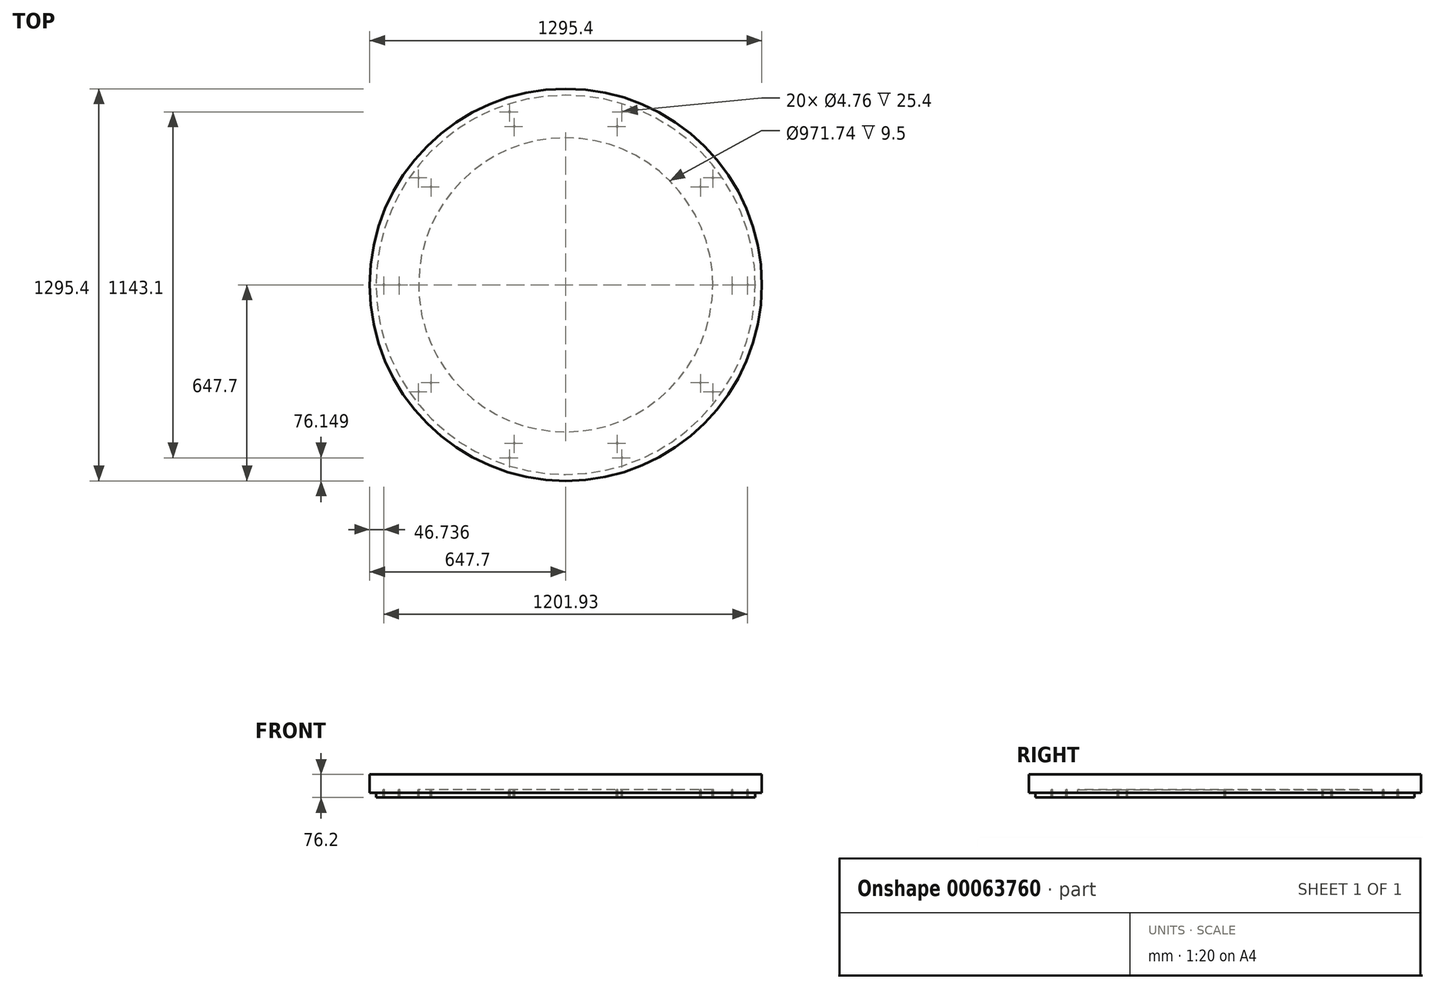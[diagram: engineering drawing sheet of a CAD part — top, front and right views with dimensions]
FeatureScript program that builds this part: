
annotation { "Feature Type Name" : "Feature", "Feature Type Description" : "" }
export const myFeature = defineFeature(function(context is Context, id is Id, definition is map)
    precondition{}
    {
        {
            assignVariable(context, id + "F0", {"name" : "H", "anyValue" : 15});
        }
        {
            assignVariable(context, id + "F1", {"name" : "S", "anyValue" : 10});
        }
        {
            var Q0;
            Q0=qCreatedBy(makeId("Top.planeOp"),FACE);
            var sketch = newSketch(context, id + "F2", { "sketchPlane" : qUnion([Q0])});
            skCircle(sketch, "E0", {"center": v(0, 0) * mm, "radius": 647.7 * mm});
            skCircle(sketch, "E1", {"center": v(0, 0) * mm, "radius": 635 * mm});
            skCircle(sketch, "E2.0", {"center": v(0, 0) * mm, "radius": 626.36 * mm});
            skSolve(sketch);
        }
        {
            var Q0;
            Q0=makeQuery(id+"F2.imprint","IMPRINT",FACE,{"disambiguationData":[TD([[makeQuery(id+"F2.imprint","IMPRINT",EDGE,{"derivedFrom":sQuery(id+"F2.wireOp",EDGE,"E1")}),1.0]])]});
            var Q1;
            Q1=sQuery(id+"F2.wireOp",EDGE,"E1");
            var Q2;
            Q2=sQuery(id+"F2.wireOp",EDGE,"E2.0");
            extrude(context, id + "F3", {"entities" : qUnion([Q0]), "surfaceEntities" : qUnion([Q1, Q2]), "depth" : (getVariable(context, 'H') - 5.5) * mm});
        }
        {
            var Q0;
            Q0=makeQuery(id+"F3.opExtrude","CAP_FACE",FACE,{"disambiguationData":[OSD([sQuery(id+"F2.wireOp",EDGE,"E1"),sQuery(id+"F2.wireOp",EDGE,"E2.0")])],"isStart":false});
            var sketch = newSketch(context, id + "F4", { "sketchPlane" : qUnion([Q0])});
            skCircle(sketch, "E3.0", {"center": v(0, 0) * mm, "radius": 626.36 * mm});
            skSolve(sketch);
        }
        {
            var Q0;
            Q0=qSketchRegion(id+"F4",true);
            extrude(context, id + "F5", {"entities" : qUnion([Q0]), "oppositeDirection" : true, "depth" : 25.4 * mm});
        }
        {
            var Q0;
            Q0=makeQuery(id+"F5.opExtrude","CAP_FACE",FACE,{"disambiguationData":[OSD([sQuery(id+"F4.wireOp",EDGE,"E3.0")])],"isStart":true});
            var sketch = newSketch(context, id + "F6", { "sketchPlane" : qUnion([Q0])});
            skLineSegment(sketch, "E4", {"start": v(-626.36, 0) * mm, "end": v(0, 0) * mm, "construction": true});
            skCircle(sketch, "E5.0", {"center": v(0, 0) * mm, "radius": 600.96 * mm, "construction": true});
            skCircle(sketch, "E6.0", {"center": v(0, 0) * mm, "radius": 550.16 * mm, "construction": true});
            skPoint(sketch, "E7", {"position": v(-600.96, 0) * mm});
            skPoint(sketch, "E8", {"position": v(-550.16, 0) * mm});
            skPoint(sketch, "E9.1.0", {"position": v(-445.1, -323.38) * mm});
            skPoint(sketch, "E9.1.1", {"position": v(-486.2, -353.24) * mm});
            skPoint(sketch, "E9.2.0", {"position": v(-170.01, -523.24) * mm});
            skPoint(sketch, "E9.2.1", {"position": v(-185.7, -571.55) * mm});
            skPoint(sketch, "E9.3.0", {"position": v(170.01, -523.24) * mm});
            skPoint(sketch, "E9.3.1", {"position": v(185.7, -571.55) * mm});
            skPoint(sketch, "E9.4.0", {"position": v(445.1, -323.38) * mm});
            skPoint(sketch, "E9.4.1", {"position": v(486.2, -353.24) * mm});
            skPoint(sketch, "E10.0.5.0", {"position": v(550.16, 0) * mm});
            skPoint(sketch, "E10.1.5.0", {"position": v(600.96, 0) * mm});
            skPoint(sketch, "E11.0.6.0", {"position": v(445.1, 323.38) * mm});
            skPoint(sketch, "E11.1.6.0", {"position": v(486.2, 353.24) * mm});
            skPoint(sketch, "E12.0.7.0", {"position": v(170.01, 523.24) * mm});
            skPoint(sketch, "E12.1.7.0", {"position": v(185.7, 571.55) * mm});
            skPoint(sketch, "E12.0.8.0", {"position": v(-170.01, 523.24) * mm});
            skPoint(sketch, "E12.1.8.0", {"position": v(-185.7, 571.55) * mm});
            skPoint(sketch, "E12.0.9.0", {"position": v(-445.1, 323.38) * mm});
            skPoint(sketch, "E12.1.9.0", {"position": v(-486.2, 353.24) * mm});
            skSolve(sketch);
        }
        {
            var Q0;
            Q0=sQuery(id+"F6.wireOp",VERTEX,"E7");
            var Q1;
            Q1=sQuery(id+"F6.wireOp",VERTEX,"E8");
            var Q2;
            Q2=sQuery(id+"F6.wireOp",VERTEX,"E9.4.1");
            var Q3;
            Q3=sQuery(id+"F6.wireOp",VERTEX,"E9.4.0");
            var Q4;
            Q4=sQuery(id+"F6.wireOp",VERTEX,"E9.3.0");
            var Q5;
            Q5=sQuery(id+"F6.wireOp",VERTEX,"E9.3.1");
            var Q6;
            Q6=sQuery(id+"F6.wireOp",VERTEX,"E9.2.0");
            var Q7;
            Q7=sQuery(id+"F6.wireOp",VERTEX,"E9.2.1");
            var Q8;
            Q8=sQuery(id+"F6.wireOp",VERTEX,"E9.1.1");
            var Q9;
            Q9=sQuery(id+"F6.wireOp",VERTEX,"E9.1.0");
            var Q10;
            Q10=sQuery(id+"F6.wireOp",VERTEX,"E10.0.5.0");
            var Q11;
            Q11=sQuery(id+"F6.wireOp",VERTEX,"E10.1.5.0");
            var Q12;
            Q12=sQuery(id+"F6.wireOp",VERTEX,"E11.1.6.0");
            var Q13;
            Q13=sQuery(id+"F6.wireOp",VERTEX,"E11.0.6.0");
            var Q14;
            Q14=sQuery(id+"F6.wireOp",VERTEX,"E12.1.9.0");
            var Q15;
            Q15=sQuery(id+"F6.wireOp",VERTEX,"E12.0.9.0");
            var Q16;
            Q16=sQuery(id+"F6.wireOp",VERTEX,"E12.1.8.0");
            var Q17;
            Q17=sQuery(id+"F6.wireOp",VERTEX,"E12.0.8.0");
            var Q18;
            Q18=sQuery(id+"F6.wireOp",VERTEX,"E12.0.7.0");
            var Q19;
            Q19=sQuery(id+"F6.wireOp",VERTEX,"E12.1.7.0");
            var Q20;
            Q20=makeQuery(id+"F5.opExtrude","SWEPT_BODY",BODY,{"disambiguationData":[OSD([sQuery(id+"F4.wireOp",EDGE,"E3.0")])]});
            hole(context, id + "F7", {"style" : HoleStyle.C_SINK, "holeDiameter" : 4.76 * mm, "cSinkDiameter" : 8.43 * mm, "endStyle" : HoleEndStyle.THROUGH, "locations" : qUnion([Q0, Q1, Q2, Q3, Q4, Q5, Q6, Q7, Q8, Q9, Q10, Q11, Q12, Q13, Q14, Q15, Q16, Q17, Q18, Q19]), "scope" : qUnion([Q20]), "cSinkAngle" : 90 * degree});
        }
        {
            var Q0;
            Q0=makeQuery(id+"F5.opExtrude","SWEPT_BODY",BODY,{"disambiguationData":[OSD([sQuery(id+"F4.wireOp",EDGE,"E3.0")])]});
            var Q1;
            Q1=qCreatedBy(makeId("Top.planeOp"),FACE);
            mirror(context, id + "F8", {"entities" : qUnion([Q0]), "mirrorPlane" : qUnion([Q1])});
        }
        {
            var Q0;
            Q0=makeQuery(id+"F8.opPattern","COPY",BODY,{"derivedFrom":makeQuery(id+"F5.opExtrude","SWEPT_BODY",BODY,{"disambiguationData":[OSD([sQuery(id+"F4.wireOp",EDGE,"E3.0")])]}),"instanceName":"1"});
            var Q1;
            Q1=makeQuery(id+"F5.opExtrude","CAP_FACE",FACE,{"disambiguationData":[OSD([sQuery(id+"F4.wireOp",EDGE,"E3.0")])],"isStart":true});
            transform(context, id + "F9", {"entities" : qUnion([Q0]), "transformType" : TransformType.TRANSLATION_3D, "dx" : 0 * mm, "dy" : 0 * mm, "dz" : (getVariable(context, 'H') - 5.5) * mm, "makeCopy" : false});
        }
        {
            var Q0;
            Q0=makeQuery(id+"F8.opPattern","COPY",FACE,{"derivedFrom":makeQuery(id+"F5.opExtrude","CAP_FACE",FACE,{"disambiguationData":[OSD([sQuery(id+"F4.wireOp",EDGE,"E3.0")])],"isStart":true}),"instanceName":"1"});
            var sketch = newSketch(context, id + "F10", { "sketchPlane" : qUnion([Q0])});
            skCircle(sketch, "E13.0", {"center": v(0, 0) * mm, "radius": 608.1 * mm, "construction": true});
            skCircle(sketch, "E14.0", {"center": v(0, 0) * mm, "radius": 571.6 * mm, "construction": true});
            skCircle(sketch, "E15.0", {"center": v(0, 0) * mm, "radius": 535.08 * mm, "construction": true});
            skLineSegment(sketch, "E16", {"start": v(0, 0) * mm, "end": v(0, 608.1) * mm, "construction": true});
            skLineSegment(sketch, "E17.0", {"start": v(22.23, 0) * mm, "end": v(22.23, 265.2) * mm, "construction": true});
            skLineSegment(sketch, "E18.0", {"start": v(-22.23, 0) * mm, "end": v(-22.23, 265.2) * mm, "construction": true});
            skPoint(sketch, "E19", {"position": v(-22.23, 571.16) * mm});
            skPoint(sketch, "E20", {"position": v(-22.23, 534.62) * mm});
            skPoint(sketch, "E21", {"position": v(22.23, 534.62) * mm});
            skPoint(sketch, "E22", {"position": v(22.23, 571.16) * mm});
            skPoint(sketch, "E23", {"position": v(22.23, 607.7) * mm});
            skPoint(sketch, "E24", {"position": v(-22.23, 607.7) * mm});
            skPoint(sketch, "E25.1.0", {"position": v(-515.32, 144.07) * mm});
            skPoint(sketch, "E25.1.1", {"position": v(-550.08, 155.36) * mm});
            skPoint(sketch, "E25.1.2", {"position": v(-584.83, 166.65) * mm});
            skPoint(sketch, "E25.1.3", {"position": v(-571.1, 208.93) * mm});
            skPoint(sketch, "E25.1.4", {"position": v(-536.34, 197.64) * mm});
            skPoint(sketch, "E25.1.5", {"position": v(-501.59, 186.34) * mm});
            skPoint(sketch, "E25.2.0", {"position": v(-296.26, -445.58) * mm});
            skPoint(sketch, "E25.2.1", {"position": v(-317.74, -475.14) * mm});
            skPoint(sketch, "E25.2.2", {"position": v(-339.22, -504.7) * mm});
            skPoint(sketch, "E25.2.3", {"position": v(-375.18, -478.58) * mm});
            skPoint(sketch, "E25.2.4", {"position": v(-353.7, -449.02) * mm});
            skPoint(sketch, "E25.2.5", {"position": v(-332.22, -419.45) * mm});
            skPoint(sketch, "E25.3.0", {"position": v(332.22, -419.45) * mm});
            skPoint(sketch, "E25.3.1", {"position": v(353.7, -449.02) * mm});
            skPoint(sketch, "E25.3.2", {"position": v(375.18, -478.58) * mm});
            skPoint(sketch, "E25.3.3", {"position": v(339.22, -504.7) * mm});
            skPoint(sketch, "E25.3.4", {"position": v(317.74, -475.14) * mm});
            skPoint(sketch, "E25.3.5", {"position": v(296.26, -445.58) * mm});
            skPoint(sketch, "E25.4.0", {"position": v(501.59, 186.34) * mm});
            skPoint(sketch, "E25.4.1", {"position": v(536.34, 197.64) * mm});
            skPoint(sketch, "E25.4.2", {"position": v(571.1, 208.93) * mm});
            skPoint(sketch, "E25.4.3", {"position": v(584.83, 166.65) * mm});
            skPoint(sketch, "E25.4.4", {"position": v(550.08, 155.36) * mm});
            skPoint(sketch, "E25.4.5", {"position": v(515.32, 144.07) * mm});
            skSolve(sketch);
        }
        {
            var Q0;
            Q0=sQuery(id+"F10.wireOp",VERTEX,"E24");
            var Q1;
            Q1=sQuery(id+"F10.wireOp",VERTEX,"E19");
            var Q2;
            Q2=sQuery(id+"F10.wireOp",VERTEX,"E20");
            var Q3;
            Q3=sQuery(id+"F10.wireOp",VERTEX,"E21");
            var Q4;
            Q4=sQuery(id+"F10.wireOp",VERTEX,"E22");
            var Q5;
            Q5=sQuery(id+"F10.wireOp",VERTEX,"E23");
            var Q6;
            Q6=sQuery(id+"F10.wireOp",VERTEX,"E25.4.0");
            var Q7;
            Q7=sQuery(id+"F10.wireOp",VERTEX,"E25.4.1");
            var Q8;
            Q8=sQuery(id+"F10.wireOp",VERTEX,"E25.4.2");
            var Q9;
            Q9=sQuery(id+"F10.wireOp",VERTEX,"E25.4.3");
            var Q10;
            Q10=sQuery(id+"F10.wireOp",VERTEX,"E25.4.4");
            var Q11;
            Q11=sQuery(id+"F10.wireOp",VERTEX,"E25.4.5");
            var Q12;
            Q12=sQuery(id+"F10.wireOp",VERTEX,"E25.3.0");
            var Q13;
            Q13=sQuery(id+"F10.wireOp",VERTEX,"E25.3.1");
            var Q14;
            Q14=sQuery(id+"F10.wireOp",VERTEX,"E25.3.2");
            var Q15;
            Q15=sQuery(id+"F10.wireOp",VERTEX,"E25.3.3");
            var Q16;
            Q16=sQuery(id+"F10.wireOp",VERTEX,"E25.3.4");
            var Q17;
            Q17=sQuery(id+"F10.wireOp",VERTEX,"E25.3.5");
            var Q18;
            Q18=sQuery(id+"F10.wireOp",VERTEX,"E25.2.2");
            var Q19;
            Q19=sQuery(id+"F10.wireOp",VERTEX,"E25.2.1");
            var Q20;
            Q20=sQuery(id+"F10.wireOp",VERTEX,"E25.2.0");
            var Q21;
            Q21=sQuery(id+"F10.wireOp",VERTEX,"E25.2.5");
            var Q22;
            Q22=sQuery(id+"F10.wireOp",VERTEX,"E25.2.4");
            var Q23;
            Q23=sQuery(id+"F10.wireOp",VERTEX,"E25.2.3");
            var Q24;
            Q24=sQuery(id+"F10.wireOp",VERTEX,"E25.1.0");
            var Q25;
            Q25=sQuery(id+"F10.wireOp",VERTEX,"E25.1.5");
            var Q26;
            Q26=sQuery(id+"F10.wireOp",VERTEX,"E25.1.1");
            var Q27;
            Q27=sQuery(id+"F10.wireOp",VERTEX,"E25.1.2");
            var Q28;
            Q28=sQuery(id+"F10.wireOp",VERTEX,"E25.1.3");
            var Q29;
            Q29=sQuery(id+"F10.wireOp",VERTEX,"E25.1.4");
            var Q30;
            Q30=makeQuery(id+"F8.opPattern","COPY",BODY,{"derivedFrom":makeQuery(id+"F5.opExtrude","SWEPT_BODY",BODY,{"disambiguationData":[OSD([sQuery(id+"F4.wireOp",EDGE,"E3.0")])]}),"instanceName":"1"});
            hole(context, id + "F11", {"style" : HoleStyle.SIMPLE, "holeDiameter" : 3.17 * mm, "endStyle" : HoleEndStyle.BLIND, "holeDepth" : 3.17 * mm, "locations" : qUnion([Q0, Q1, Q2, Q3, Q4, Q5, Q6, Q7, Q8, Q9, Q10, Q11, Q12, Q13, Q14, Q15, Q16, Q17, Q18, Q19, Q20, Q21, Q22, Q23, Q24, Q25, Q26, Q27, Q28, Q29]), "scope" : qUnion([Q30])});
        }
        {
            var Q0;
            Q0=makeQuery(id+"F8.opPattern","COPY",FACE,{"derivedFrom":makeQuery(id+"F5.opExtrude","CAP_FACE",FACE,{"disambiguationData":[OSD([sQuery(id+"F4.wireOp",EDGE,"E3.0")])],"isStart":false}),"instanceName":"1"});
            var sketch = newSketch(context, id + "F12", { "sketchPlane" : qUnion([Q0])});
            skCircle(sketch, "E26", {"center": v(0, 0) * mm, "radius": 485.87 * mm});
            skSolve(sketch);
        }
        {
            var Q0;
            Q0=qSketchRegion(id+"F12",true);
            extrude(context, id + "F13", {"entities" : qUnion([Q0]), "operationType" : NewBodyOperationType.REMOVE, "oppositeDirection" : true, "depth" : 25.4 * mm});
        }
        {
            var Q0;
            Q0=makeQuery(id+"F8.opPattern","COPY",FACE,{"derivedFrom":makeQuery(id+"F5.opExtrude","CAP_FACE",FACE,{"disambiguationData":[OSD([sQuery(id+"F4.wireOp",EDGE,"E3.0")])],"isStart":false}),"instanceName":"1"});
            var sketch = newSketch(context, id + "F14", { "sketchPlane" : qUnion([Q0])});
            skLineSegment(sketch, "E27", {"start": v(-600.96, 0) * mm, "end": v(-550.16, 0) * mm, "construction": true});
            skLineSegment(sketch, "E28.0", {"start": v(-626.36, 12.7) * mm, "end": v(-524.76, 12.7) * mm});
            skLineSegment(sketch, "E29.0", {"start": v(-626.36, -12.7) * mm, "end": v(-524.76, -12.7) * mm});
            skLineSegment(sketch, "E30", {"start": v(-626.36, -12.7) * mm, "end": v(-626.36, 12.7) * mm});
            skLineSegment(sketch, "E31", {"start": v(-524.76, -12.7) * mm, "end": v(-524.76, 12.7) * mm});
            skSolve(sketch);
        }
        {
            var Q0;
            Q0=qSketchRegion(id+"F14",true);
            extrude(context, id + "F15", {"entities" : qUnion([Q0]), "depth" : (getVariable(context, 'H') - 7.5) * mm});
        }
        {
            var Q0;
            Q0=makeQuery(id+"F15.opExtrude","SWEPT_BODY",BODY,{"disambiguationData":[OSD([sQuery(id+"F14.wireOp",EDGE,"E28.0"),sQuery(id+"F14.wireOp",EDGE,"E29.0"),sQuery(id+"F14.wireOp",EDGE,"E30"),sQuery(id+"F14.wireOp",EDGE,"E31")])]});
            var Q1;
            Q1=makeQuery(id+"F8.opPattern","COPY",EDGE,{"derivedFrom":makeQuery(id+"F5.opExtrude","CAP_EDGE",EDGE,{"disambiguationData":[OSD([sQuery(id+"F4.wireOp",EDGE,"E3.0")])],"isStart":false}),"instanceName":"1"});
            circularPattern(context, id + "F16", {"entities" : qUnion([Q0]), "axis" : qUnion([Q1]), "angle" : 360 * degree, "instanceCount" : getVariable(context, 'S'), "equalSpace" : true});
        }
        {
            var Q0;
            Q0=makeQuery(id+"F2.imprint","IMPRINT",FACE,{"disambiguationData":[TD([[makeQuery(id+"F2.imprint","IMPRINT",EDGE,{"derivedFrom":sQuery(id+"F2.wireOp",EDGE,"E0")}),1.0]])]});
            extrude(context, id + "F17", {"entities" : qUnion([Q0]), "depth" : (getVariable(context, 'H') - 5.5) * mm});
        }
        {
            var Q0;
            Q0=makeQuery(id+"F17.opExtrude","CAP_FACE",FACE,{"disambiguationData":[OSD([sQuery(id+"F2.wireOp",EDGE,"E0"),sQuery(id+"F2.wireOp",EDGE,"E1")])],"isStart":false});
            var sketch = newSketch(context, id + "F18", { "sketchPlane" : qUnion([Q0])});
            skCircle(sketch, "E32.0", {"center": v(0, 0) * mm, "radius": 647.7 * mm});
            skSolve(sketch);
        }
        {
            var Q0;
            Q0=qSketchRegion(id+"F18",true);
            extrude(context, id + "F19", {"entities" : qUnion([Q0]), "operationType" : NewBodyOperationType.ADD, "depth" : 50.8 * mm});
        }
    });
